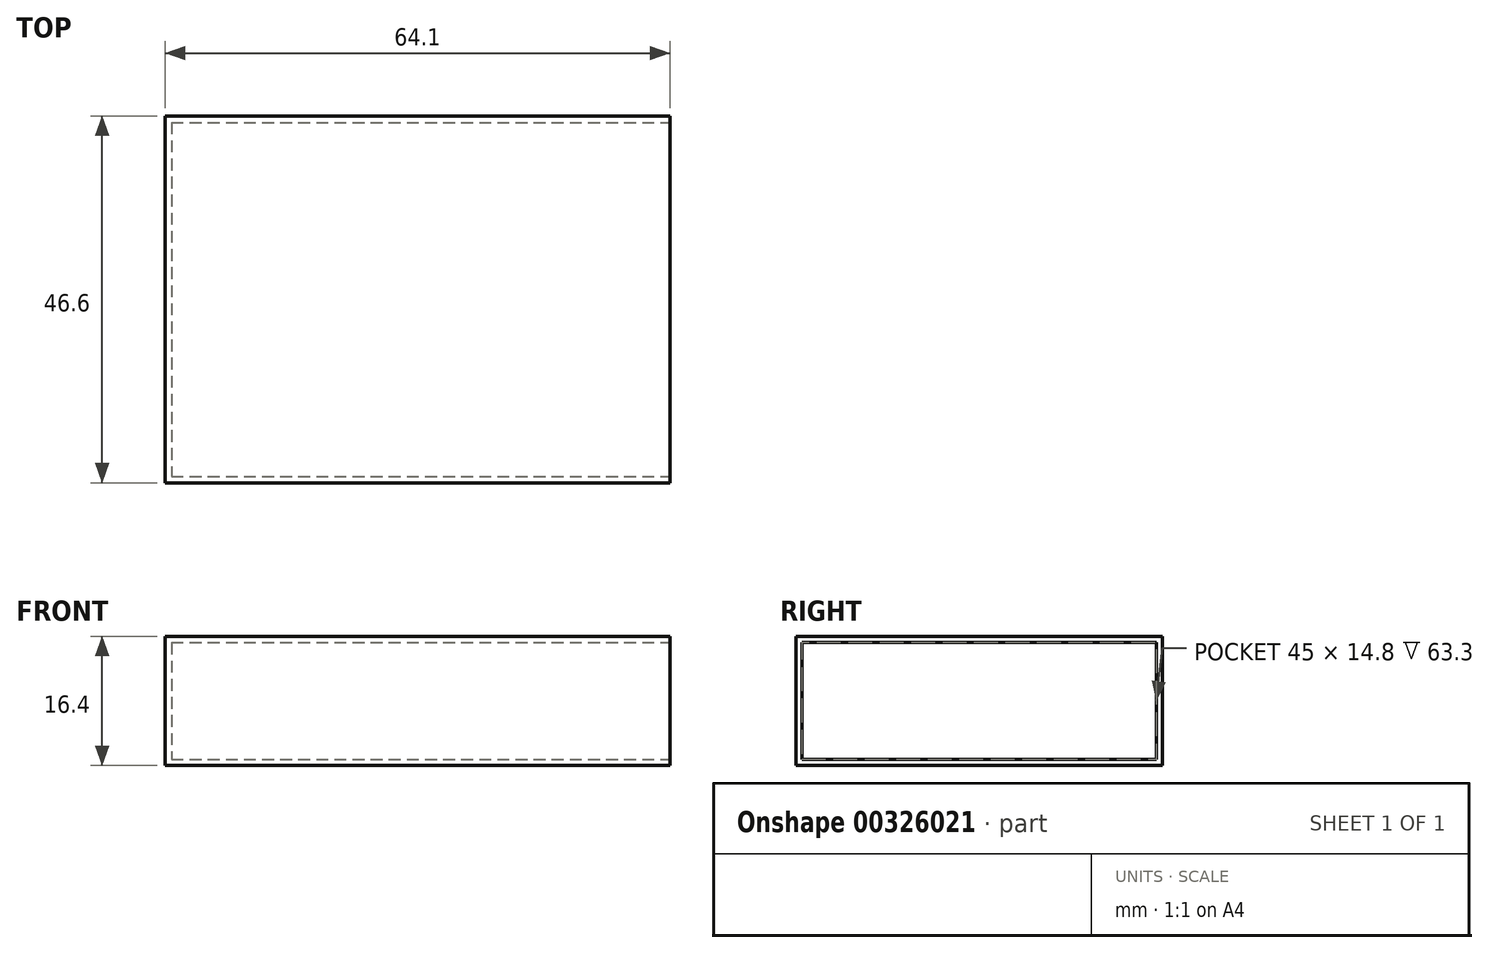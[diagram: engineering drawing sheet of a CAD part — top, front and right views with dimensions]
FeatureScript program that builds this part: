
annotation { "Feature Type Name" : "Feature", "Feature Type Description" : "" }
export const myFeature = defineFeature(function(context is Context, id is Id, definition is map)
    precondition{}
    {
        {
            var Q0;
            Q0=qCreatedBy(makeId("Top.planeOp"),FACE);
            var sketch = newSketch(context, id + "F0", { "sketchPlane" : qUnion([Q0])});
            skLineSegment(sketch, "E0.bottom", {"start": v(-61.8, -15.51) * mm, "end": v(0.9, -15.51) * mm, "construction": true});
            skLineSegment(sketch, "E0.top", {"start": v(-61.8, -59.91) * mm, "end": v(0.9, -59.91) * mm, "construction": true});
            skLineSegment(sketch, "E0.left", {"start": v(-61.8, -15.51) * mm, "end": v(-61.8, -59.91) * mm, "construction": true});
            skLineSegment(sketch, "E0.right", {"start": v(0.9, -15.51) * mm, "end": v(0.9, -59.91) * mm, "construction": true});
            skLineSegment(sketch, "E1.0", {"start": v(-62.1, -15.21) * mm, "end": v(-62.1, -60.21) * mm});
            skLineSegment(sketch, "E1.1", {"start": v(-62.1, -15.21) * mm, "end": v(1.2, -15.21) * mm});
            skLineSegment(sketch, "E1.2", {"start": v(1.2, -15.21) * mm, "end": v(1.2, -60.21) * mm});
            skLineSegment(sketch, "E1.3", {"start": v(-62.1, -60.21) * mm, "end": v(1.2, -60.21) * mm});
            skLineSegment(sketch, "E2.0", {"start": v(-62.9, -14.41) * mm, "end": v(-62.9, -61.01) * mm});
            skLineSegment(sketch, "E2.1", {"start": v(-62.9, -14.41) * mm, "end": v(2, -14.41) * mm});
            skLineSegment(sketch, "E2.2", {"start": v(2, -14.41) * mm, "end": v(2, -61.01) * mm});
            skLineSegment(sketch, "E2.3", {"start": v(-62.9, -61.01) * mm, "end": v(2, -61.01) * mm});
            skSolve(sketch);
        }
        {
            var Q0;
            Q0=makeQuery(id+"F0.imprint","IMPRINT",FACE,{"disambiguationData":[TD([[makeQuery(id+"F0.imprint","IMPRINT",EDGE,{"derivedFrom":sQuery(id+"F0.wireOp",EDGE,"E1.0")}),-1.0]])]});
            var Q1;
            Q1=makeQuery(id+"F0.imprint","IMPRINT",FACE,{"disambiguationData":[TD([[makeQuery(id+"F0.imprint","IMPRINT",EDGE,{"derivedFrom":sQuery(id+"F0.wireOp",EDGE,"E1.0")}),1.0]])]});
            extrude(context, id + "F1", {"entities" : qUnion([Q0, Q1]), "oppositeDirection" : true, "depth" : 0.8 * mm});
        }
        {
            var Q0;
            Q0=makeQuery(id+"F0.imprint","IMPRINT",FACE,{"disambiguationData":[TD([[makeQuery(id+"F0.imprint","IMPRINT",EDGE,{"derivedFrom":sQuery(id+"F0.wireOp",EDGE,"E1.0")}),-1.0]])]});
            extrude(context, id + "F2", {"entities" : qUnion([Q0]), "operationType" : NewBodyOperationType.ADD, "depth" : 14.8 * mm});
        }
        {
            var Q0;
            Q0=makeQuery(id+"F2.opExtrude","CAP_FACE",FACE,{"disambiguationData":[OSD([sQuery(id+"F0.wireOp",EDGE,"E1.0"),sQuery(id+"F0.wireOp",EDGE,"E1.1"),sQuery(id+"F0.wireOp",EDGE,"E1.2"),sQuery(id+"F0.wireOp",EDGE,"E1.3"),sQuery(id+"F0.wireOp",EDGE,"E2.0"),sQuery(id+"F0.wireOp",EDGE,"E2.1"),sQuery(id+"F0.wireOp",EDGE,"E2.2"),sQuery(id+"F0.wireOp",EDGE,"E2.3")])],"isStart":false});
            var sketch = newSketch(context, id + "F3", { "sketchPlane" : qUnion([Q0])});
            skLineSegment(sketch, "E3.0", {"start": v(-62.9, -61.01) * mm, "end": v(2, -61.01) * mm});
            skLineSegment(sketch, "E4.0", {"start": v(2, -14.41) * mm, "end": v(2, -61.01) * mm});
            skLineSegment(sketch, "E5.0", {"start": v(-62.9, -14.41) * mm, "end": v(2, -14.41) * mm});
            skLineSegment(sketch, "E6.0", {"start": v(-62.9, -14.41) * mm, "end": v(-62.9, -61.01) * mm});
            skSolve(sketch);
        }
        {
            var Q0;
            Q0=makeQuery(id+"F3.imprint","IMPRINT",FACE,{"disambiguationData":[TD([[makeQuery(id+"F3.imprint","IMPRINT",EDGE,{"derivedFrom":makeQuery(id+"F2.opExtrude","CAP_EDGE",EDGE,{"disambiguationData":[OSD([sQuery(id+"F0.wireOp",EDGE,"E1.0")])],"isStart":false})}),1.0]])]});
            var Q1;
            Q1=makeQuery(id+"F3.imprint","IMPRINT",FACE,{"disambiguationData":[TD([[makeQuery(id+"F3.imprint","IMPRINT",EDGE,{"derivedFrom":sQuery(id+"F3.wireOp",EDGE,"E3.0")}),1.0]])]});
            extrude(context, id + "F4", {"entities" : qUnion([Q0, Q1]), "operationType" : NewBodyOperationType.ADD, "depth" : 0.8 * mm});
        }
        {
            var Q0;
            {var subQ0=sQuery(id+"F0.wireOp",EDGE,"E2.2");Q0=makeQuery(id+"F4.boolean.opBoolean","MERGE",FACE,{"derivedFrom":[makeQuery(id+"F2.boolean.opBoolean","MERGE",FACE,{"derivedFrom":[makeQuery(id+"F1.opExtrude","SWEPT_FACE",FACE,{"disambiguationData":[OSD([subQ0])]}),makeQuery(id+"F2.opExtrude","SWEPT_FACE",FACE,{"disambiguationData":[OSD([subQ0])]})]}),makeQuery(id+"F4.opExtrude","SWEPT_FACE",FACE,{"disambiguationData":[OSD([sQuery(id+"F3.wireOp",EDGE,"E4.0")])]})]});}
            extrude(context, id + "F5", {"entities" : qUnion([Q0]), "operationType" : NewBodyOperationType.REMOVE, "oppositeDirection" : true, "depth" : 0.8 * mm});
        }
    });
